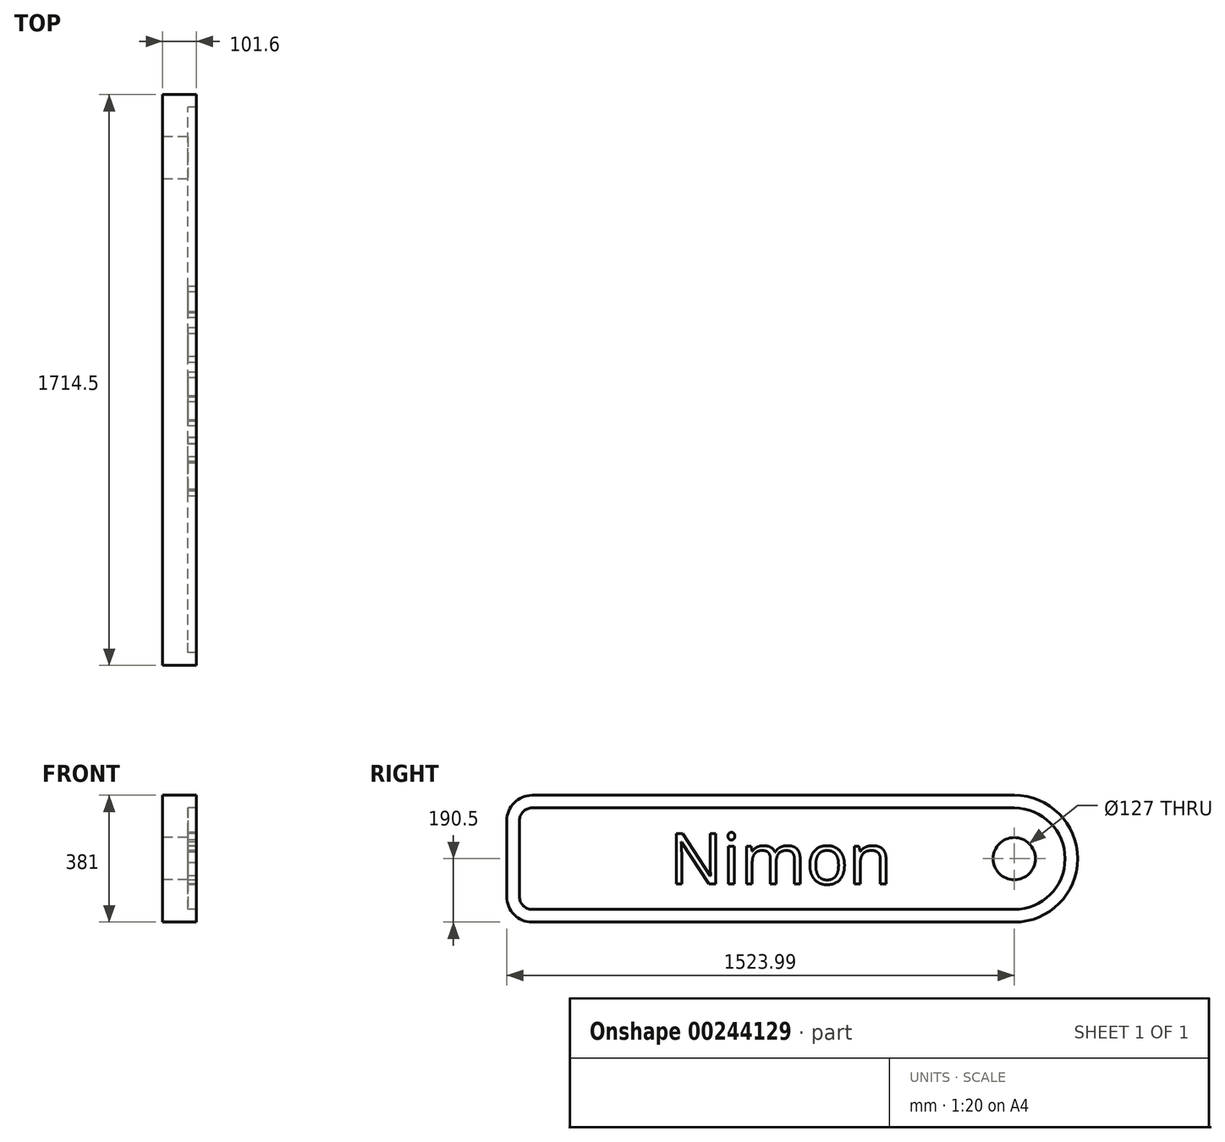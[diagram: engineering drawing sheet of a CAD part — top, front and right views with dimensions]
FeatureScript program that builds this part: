
annotation { "Feature Type Name" : "Feature", "Feature Type Description" : "" }
export const myFeature = defineFeature(function(context is Context, id is Id, definition is map)
    precondition{}
    {
        {
            var Q0;
            Q0=qCreatedBy(makeId("Right.planeOp"),FACE);
            var sketch = newSketch(context, id + "F0", { "sketchPlane" : qUnion([Q0])});
            skLineSegment(sketch, "E0.bottom", {"start": v(-681.95, 190.5) * mm, "end": v(765.85, 190.5) * mm});
            skLineSegment(sketch, "E0.top", {"start": v(-681.95, -190.5) * mm, "end": v(765.85, -190.5) * mm});
            skLineSegment(sketch, "E0.left", {"start": v(-758.15, 114.3) * mm, "end": v(-758.15, -114.3) * mm});
            skPoint(sketch, "E1.visualSharp", {"position": v(-758.15, 190.5) * mm});
            skArc(sketch, "E1.filletArc", {"start": v(-681.95, 190.5) * mm, "mid": v(-735.84, 168.18) * mm, "end": v(-758.15, 114.3) * mm});
            skPoint(sketch, "E2.visualSharp", {"position": v(-758.15, -190.5) * mm});
            skArc(sketch, "E2.filletArc", {"start": v(-758.15, -114.3) * mm, "mid": v(-735.84, -168.18) * mm, "end": v(-681.95, -190.5) * mm});
            skArc(sketch, "E3", {"start": v(765.85, -190.5) * mm, "mid": v(956.35, 0) * mm, "end": v(765.85, 190.5) * mm});
            skCircle(sketch, "E4", {"center": v(765.85, 0) * mm, "radius": 63.5 * mm});
            skSolve(sketch);
        }
        {
            var Q0;
            Q0 = qSketchRegion(id + "F0", true);
            extrude(context, id + "F1", {"entities" : qUnion([Q0]), "depth" : 76.2 * mm});
        }
        {
            var Q0;
            Q0=makeQuery(id+"F1.opExtrude","CAP_FACE",FACE,{"disambiguationData":[OSD([sQuery(id+"F0.wireOp",EDGE,"E0.bottom"),sQuery(id+"F0.wireOp",EDGE,"E0.top"),sQuery(id+"F0.wireOp",EDGE,"E0.left"),sQuery(id+"F0.wireOp",EDGE,"E1.filletArc"),sQuery(id+"F0.wireOp",EDGE,"E2.filletArc"),sQuery(id+"F0.wireOp",EDGE,"E3"),sQuery(id+"F0.wireOp",EDGE,"E4")])],"isStart":false});
            var sketch = newSketch(context, id + "F2", { "sketchPlane" : qUnion([Q0])});
            skText(sketch, "E5", { "text": "Nimon", "fontName": "OpenSans-Regular.ttf"});
            const initialGuessF2  = {"E5": [-0.26995, -0.0762, 1, 0, 0.1524]};
            skSetInitialGuess(sketch, initialGuessF2);
            skSolve(sketch);
        }
        {
            var Q0;
            Q0 = qSketchRegion(id + "F2", true);
            extrude(context, id + "F3", {"entities" : qUnion([Q0]), "operationType" : NewBodyOperationType.ADD, "depth" : 25.4 * mm});
        }
        {
            var Q0;
            {var subQ0=sQuery(id+"F0.wireOp",EDGE,"E0.left");var subQ1=sQuery(id+"F0.wireOp",EDGE,"E4");var subQ2=sQuery(id+"F0.wireOp",EDGE,"E3");var subQ3=sQuery(id+"F0.wireOp",EDGE,"E2.filletArc");var subQ4=sQuery(id+"F0.wireOp",EDGE,"E0.bottom");var subQ5=sQuery(id+"F0.wireOp",EDGE,"E1.filletArc");var subQ6=sQuery(id+"F0.wireOp",EDGE,"E0.top");Q0=makeQuery(id+"F3.boolean.opBoolean","SPLIT",FACE,{"disambiguationData":[TD([makeQuery(id+"F1.opExtrude","SWEPT_FACE",FACE,{"disambiguationData":[OSD([subQ4])]})])],"derivedFrom":makeQuery(id+"F1.opExtrude","CAP_FACE",FACE,{"disambiguationData":[OSD([subQ4,subQ6,subQ0,subQ5,subQ3,subQ2,subQ1])],"isStart":false})});}
            var sketch = newSketch(context, id + "F4", { "sketchPlane" : qUnion([Q0])});
            skArc(sketch, "E6.0", {"start": v(-681.95, 152.4) * mm, "mid": v(-708.9, 141.24) * mm, "end": v(-720.05, 114.3) * mm});
            skArc(sketch, "E6.1", {"start": v(-720.05, -114.3) * mm, "mid": v(-708.9, -141.24) * mm, "end": v(-681.95, -152.4) * mm});
            skLineSegment(sketch, "E6.2", {"start": v(-681.95, -152.4) * mm, "end": v(765.85, -152.4) * mm});
            skLineSegment(sketch, "E6.3", {"start": v(-720.05, 114.3) * mm, "end": v(-720.05, -114.3) * mm});
            skArc(sketch, "E6.4", {"start": v(765.85, -152.4) * mm, "mid": v(918.25, 0) * mm, "end": v(765.85, 152.4) * mm});
            skLineSegment(sketch, "E6.5", {"start": v(765.85, 152.4) * mm, "end": v(-681.95, 152.4) * mm});
            skSolve(sketch);
        }
        {
            var Q0;
            Q0=makeQuery(id+"F4.imprint","IMPRINT",FACE,{"disambiguationData":[TD([[makeQuery(id+"F4.imprint","IMPRINT",EDGE,{"derivedFrom":sQuery(id+"F4.wireOp",EDGE,"E6.0")}),-1.0]])]});
            extrude(context, id + "F5", {"entities" : qUnion([Q0]), "operationType" : NewBodyOperationType.ADD, "depth" : 25.4 * mm});
        }
    });
